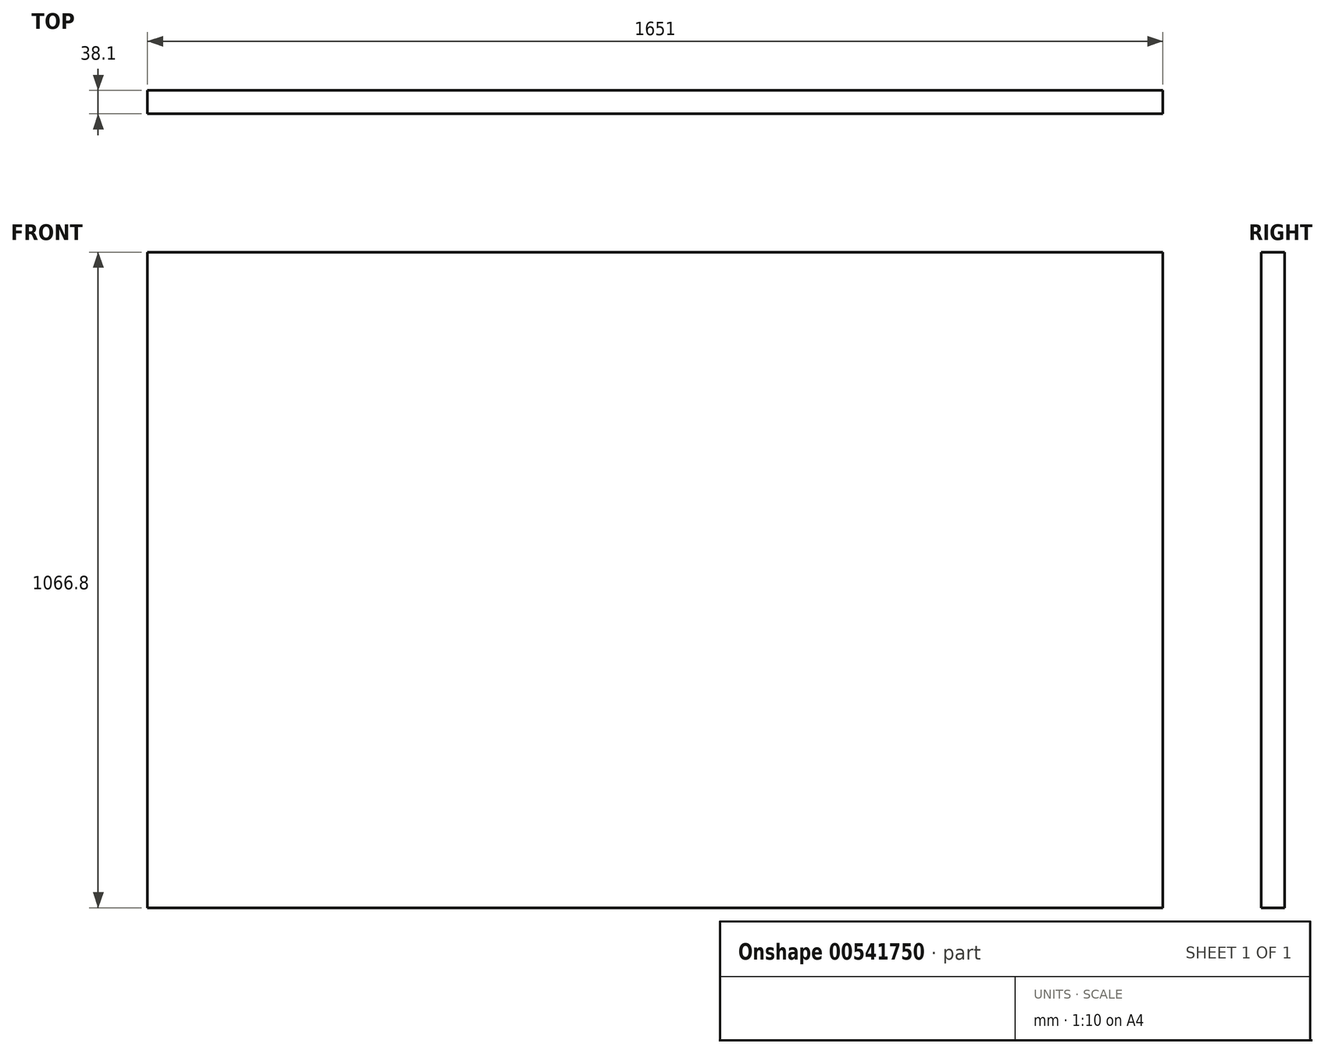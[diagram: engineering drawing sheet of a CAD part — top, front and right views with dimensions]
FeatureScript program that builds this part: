
annotation { "Feature Type Name" : "Feature", "Feature Type Description" : "" }
export const myFeature = defineFeature(function(context is Context, id is Id, definition is map)
    precondition{}
    {
        {
            var Q0;
            Q0=qCreatedBy(makeId("Front.planeOp"),FACE);
            var sketch = newSketch(context, id + "F0", { "sketchPlane" : qUnion([Q0])});
            skLineSegment(sketch, "E0.bottom", {"start": v(825.5, 533.4) * mm, "end": v(-825.5, 533.4) * mm});
            skLineSegment(sketch, "E0.top", {"start": v(825.5, -533.4) * mm, "end": v(-825.5, -533.4) * mm});
            skLineSegment(sketch, "E0.left", {"start": v(825.5, 533.4) * mm, "end": v(825.5, -533.4) * mm});
            skLineSegment(sketch, "E0.right", {"start": v(-825.5, 533.4) * mm, "end": v(-825.5, -533.4) * mm});
            skPoint(sketch, "E0.middle", {"position": v(0, 0) * mm});
            skSolve(sketch);
        }
        {
            var Q0;
            Q0=makeQuery(id+"F0.imprint","IMPRINT",FACE,{"disambiguationData":[TD([[makeQuery(id+"F0.imprint","IMPRINT",EDGE,{"derivedFrom":sQuery(id+"F0.wireOp",EDGE,"E0.bottom")}),1.0]])]});
            extrude(context, id + "F1", {"entities" : qUnion([Q0]), "depth" : 38.1 * mm, "offsetDistance" : 25.4 * mm});
        }
    });
